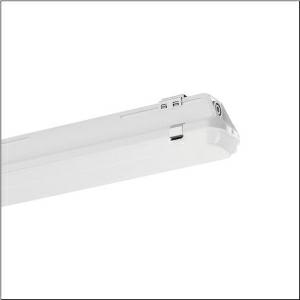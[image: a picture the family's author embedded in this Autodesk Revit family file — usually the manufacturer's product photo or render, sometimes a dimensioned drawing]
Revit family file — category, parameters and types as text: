
# Revit family: monsun_r__11_51fp109p440h_ab1f
name_source: partatom
category: Lighting Fixtures
units: mm (PartAtom-declared; Revit-internal decimal feet)

## family parameters
Cut with Voids When Loaded = No
Host = Face
Light Source = No
Part Type = Normal
Room Calculation Point = No
Round Connector Dimension = Use Diameter
Shared = No

## types (1)
- Monsun® 11 (1 x LED, 4120 lm, 22.9 W, 4000K)
    Apparent Load = 23 VA
    CIE Flux Codes = 47 77 93 94 100
    Color Rendering = 80
    Color Temperature = 4000K
    Default Elevation = 1800 mm
    Description = Monsun® 11, damp-proof luminaire, chain hanger, primary optical cover: enclosure, of PMMA, light emission: direct distribution, primary light characteristic: symmetric, installation type: suspended mounting, surface-mounted, horizontal mounting, vertical mounting, LED, rated luminous flux: 4.120lm, luminous efficacy: 180lm/W, light colour: 840, colour temperature: 4000K, control gear: ON/OFF, CLOi, with terminal, 3-pole, max. 2.5mm², mains connection: 220..240V, AC, 50/60Hz, start of lifetime: 23W, end of service life: 25W, luminaire housing, of glass-fibre reinforced polyester, uncoated, bright grey, incl. chain hanger, length: 1.590mm, width: 90mm, height: 88mm, clip for enclosure, of stainless steel (V2A), ceiling mounting element, of stainless steel (V2A), chain hanger, of stainless steel (V2A), protection rating (complete): IP66, insulation class (complete): insulation class I (protective earthing), certification: CE, ENEC, VDE, UKCA, protection symbol: D, impact resistance: IK04, permissible operating ambient temperature: -35..+40°C, standard: EN 50419, EN 60598-2-1, no direct snow, no direct sun, no direct rain, for indoor or canopied outdoor use, corresponds to IFS (International Featured Standards) requirements for safety and quality in the food industry, contact your sales advisor before using the luminaires in applications with unclear chemical exposure, large temperature fluctuations or condensation-forming humidity, LABS conformity tested according to VDMA 24364:2018-05, packaging unit: 1 piece
    Height = 89 mm
    Lamp = 1 x LED
    Lamp Light Flux = 4120 lm
    Lamp Power = 22.9 W
    Lamp count = 1
    Length = 1590 mm
    Luminous efficacy = 180 lm/W
    Manufacturer = Siteco
    ModVariant = No
    Model = 51FP109P440H
    Mounting Place = Ceiling
    Mounting Type = Surface mounted
    Number of Poles = 1
    OnlyDefault = Yes
    Power Factor = 1
    Product Name = Monsun® 11
    Product group = damp-proof luminaire
    ProductGroupID = 301
    Protection Class = Protection class I
    Protection Degree = IP 66
    RLX_Detail_Level = 1
    RLX_Emergency_Light_Flux = 0 lm
    RLX_Emergency_Type = 0
    RLX_Emergency_Type_DB = No
    RlxData = <blob elided: 88609 chars, md5=a51a76c8>
    Socket = socket
    Standby Power = 0 W
    System Light Flux = 4120 lm
    System Power = 23 W
    Type Comments = Product without accessories
    Type Image = l_1349237.jpg
    URL = http://relux.com
    VarID = ---
    Voltage = 0 V
    Weight = 0.00 kg
    Width = 90 mm

## geometry (parser evidence)
native form markers: Blend x4, Sweep x14
no freeform markers — native parametric forms only
